# Revit family: Urinal_Screen-Privada-Floor_Anchored updated
name_source: partatom
category: Specialty Equipment
revit_build: Autodesk Revit LT 2016 (Build: 20150220_1215(x64)
units: mm (PartAtom-declared; Revit-internal decimal feet)

## family parameters
Always vertical = No
Cut with Voids When Loaded = No
OmniClass Number = 23.40.20.21
OmniClass Title = Toilet and Bath Specialties
Part Type = Normal
Room Calculation Point = No
Round Connector Dimension = Use Diameter
Shared = Yes
Work Plane-Based = Yes

## types (1)
- Privada Urinal Screen
    ATS URL = http://www.atsspec.net
    Assembly Code = E2010
    Default Elevation = 0"
    Description = Privada Urinal Screen, lengths from 1'-6" to  2'-0"
    Hardware Material = Aluminum-Privada-Matte
    Height = 72"
    Installation Type = Floor-Anchored
    Length = 24"
    Manufacturer = Privada
    Masterformat Number = 10 22 00
    Masterformat Title = 10 22 00
    Material = Aluminum-Privada-Satin
    Model = Privada Urinal Screen
    Omniclass Table 23 Code = 23.40.20.21
    Omniclass Table 23 Title = Toilet and Bath Specialties
    URL = http://www.privadapartitions.com
    Warranty Information = 10 Year Warranty

## geometry (parser evidence)
native form markers: Sweep x2
no freeform markers — native parametric forms only
